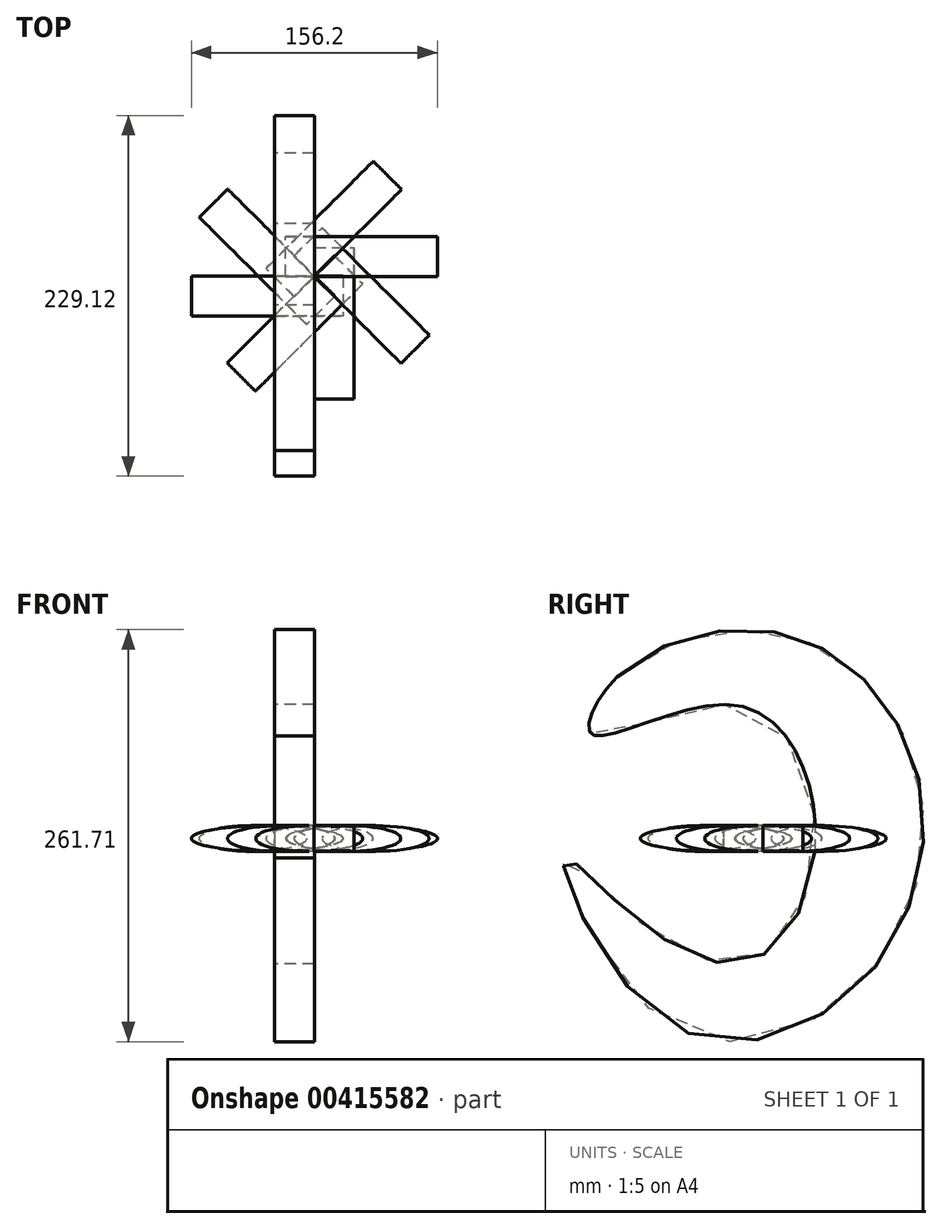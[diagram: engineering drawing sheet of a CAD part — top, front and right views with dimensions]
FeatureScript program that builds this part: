
annotation { "Feature Type Name" : "Feature", "Feature Type Description" : "" }
export const myFeature = defineFeature(function(context is Context, id is Id, definition is map)
    precondition{}
    {
        {
            var Q0;
            Q0=qCreatedBy(makeId("Front.planeOp"),FACE);
            var sketch = newSketch(context, id + "F0", { "sketchPlane" : qUnion([Q0])});
            skEllipse(sketch, "E0", {"center": v(0, 0) * mm, "majorRadius": 48.17 * mm, "minorRadius": 8.15 * mm, "majorAxis": v(0, 1)});
            skSolve(sketch);
        }
        {
            var Q0;
            Q0=makeQuery(id+"F0.imprint","IMPRINT",FACE,{"disambiguationData":[TD([[makeQuery(id+"F0.imprint","IMPRINT",EDGE,{"derivedFrom":sQuery(id+"F0.wireOp",EDGE,"E0")}),1.0]])]});
            extrude(context, id + "F1", {"entities" : qUnion([Q0]), "depth" : 25.4 * mm});
        }
        {
            var Q0;
            Q0=qCreatedBy(makeId("Right.planeOp"),FACE);
            var sketch = newSketch(context, id + "F2", { "sketchPlane" : qUnion([Q0])});
            skFitSpline(sketch, "E1", {"points": [v(-102.1, 106.6) * mm, v(-18.08, 136.55) * mm, v(50.36, 109.03) * mm, v(92.17, 25.82) * mm, v(51, -89.73) * mm, v(-71.06, -112.35) * mm, v(-135.92, -9.36) * mm, v(-101.67, -37.08) * mm, v(-19.67, -74.55) * mm, v(23.93, 0) * mm, v(-25.11, 88.29) * mm, v(-117.44, 69.86) * mm, v(-102.1, 106.6) * mm]});
            skSolve(sketch);
        }
        {
            var Q0;
            Q0=makeQuery(id+"F2.imprint","IMPRINT",FACE,{"disambiguationData":[TD([[makeQuery(id+"F2.imprint","IMPRINT",EDGE,{"derivedFrom":sQuery(id+"F2.wireOp",EDGE,"E1")}),-1.0]])]});
            extrude(context, id + "F3", {"entities" : qUnion([Q0]), "operationType" : NewBodyOperationType.ADD, "depth" : 25.4 * mm});
        }
        {
            var Q0;
            Q0=makeQuery(id+"F3.opExtrude","CAP_FACE",FACE,{"disambiguationData":[OSD([sQuery(id+"F2.wireOp",EDGE,"E1")])],"isStart":false});
            var sketch = newSketch(context, id + "F4", { "sketchPlane" : qUnion([Q0])});
            skSolve(sketch);
        }
        {
            var Q0;
            Q0=qCreatedBy(makeId("Top.planeOp"),FACE);
            var sketch = newSketch(context, id + "F5", { "sketchPlane" : qUnion([Q0])});
            skLineSegment(sketch, "E2", {"start": v(0, 0) * mm, "end": v(0, -76.37) * mm});
            skSolve(sketch);
        }
        {
            var Q0;
            Q0=makeQuery(id+"F1.opExtrude","SWEPT_BODY",BODY,{"disambiguationData":[OSD([sQuery(id+"F0.wireOp",EDGE,"E0")])]});
            var Q1;
            Q1=sQuery(id+"F5.wireOp",EDGE,"E2");
            transform(context, id + "F6", {"entities" : qUnion([Q0]), "transformType" : TransformType.ROTATION, "transformAxis" : qUnion([Q1]), "angle" : 90 * degree, "makeCopy" : false});
        }
        {
            var Q0;
            Q0=makeQuery(id+"F4.imprint","IMPRINT",FACE,{"disambiguationData":[TD([[makeQuery(id+"F4.imprint","IMPRINT",EDGE,{"derivedFrom":makeQuery(id+"F3.opExtrude","CAP_EDGE",EDGE,{"disambiguationData":[OSD([sQuery(id+"F2.wireOp",EDGE,"E1")])],"isStart":false})}),-1.0]])]});
            var sketch = newSketch(context, id + "F7", { "sketchPlane" : qUnion([Q0])});
            skLineSegment(sketch, "E3", {"start": v(-9.26, 18.75) * mm, "end": v(-9.26, 119.93) * mm});
            skSolve(sketch);
        }
        {
            var Q0;
            Q0=makeQuery(id+"F1.opExtrude","SWEPT_BODY",BODY,{"disambiguationData":[OSD([sQuery(id+"F0.wireOp",EDGE,"E0")])]});
            var Q1;
            Q1=sQuery(id+"F7.wireOp",EDGE,"E3");
            transform(context, id + "F8", {"entities" : qUnion([Q0]), "transformType" : TransformType.ROTATION, "transformAxis" : qUnion([Q1]), "angle" : 90 * degree, "makeCopy" : false});
        }
        {
            var Q0;
            Q0=makeQuery(id+"F1.opExtrude","SWEPT_BODY",BODY,{"disambiguationData":[OSD([sQuery(id+"F0.wireOp",EDGE,"E0")])]});
            transform(context, id + "F9", {"entities" : qUnion([Q0]), "transformType" : TransformType.TRANSLATION_3D, "dx" : -15.94 * mm, "dy" : 55.33 * mm, "dz" : 3.94 * mm, "makeCopy" : false});
        }
        {
            var Q0;
            Q0=makeQuery(id+"F1.opExtrude","SWEPT_BODY",BODY,{"disambiguationData":[OSD([sQuery(id+"F0.wireOp",EDGE,"E0")])]});
            var Q1;
            Q1=sQuery(id+"F7.wireOp",EDGE,"E3");
            circularPattern(context, id + "F10", {"entities" : qUnion([Q0]), "axis" : qUnion([Q1]), "angle" : 360 * degree, "instanceCount" : 8, "equalSpace" : true});
        }
    });
